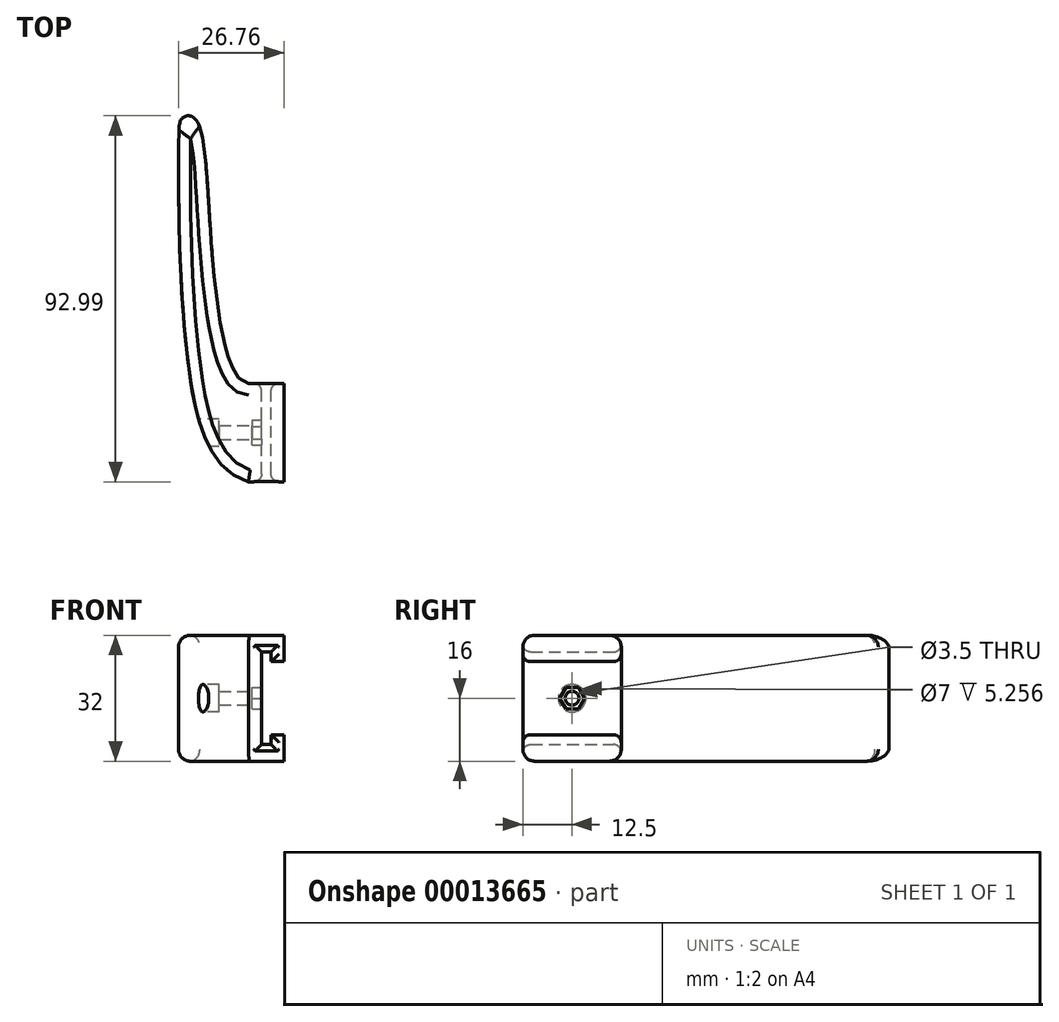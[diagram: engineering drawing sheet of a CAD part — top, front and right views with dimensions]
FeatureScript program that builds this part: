
annotation { "Feature Type Name" : "Feature", "Feature Type Description" : "" }
export const myFeature = defineFeature(function(context is Context, id is Id, definition is map)
    precondition{}
    {
        {
            var Q0;
            Q0=qCreatedBy(makeId("Front.planeOp"),FACE);
            var sketch = newSketch(context, id + "F0", { "sketchPlane" : qUnion([Q0])});
            skLineSegment(sketch, "E0", {"start": v(-4.57, 0) * mm, "end": v(-4.57, 16) * mm});
            skLineSegment(sketch, "E1", {"start": v(-4.57, 16) * mm, "end": v(4.43, 16) * mm});
            skLineSegment(sketch, "E2", {"start": v(4.43, 16) * mm, "end": v(4.43, 9.3) * mm});
            skLineSegment(sketch, "E3", {"start": v(4.43, 9.3) * mm, "end": v(1.18, 9.3) * mm});
            skLineSegment(sketch, "E4", {"start": v(1.18, 9.3) * mm, "end": v(1.18, 11.75) * mm});
            skLineSegment(sketch, "E5", {"start": v(1.18, 11.75) * mm, "end": v(-1.22, 11.75) * mm});
            skLineSegment(sketch, "E6", {"start": v(-1.22, 11.75) * mm, "end": v(-1.22, 0) * mm});
            skLineSegment(sketch, "E7", {"start": v(-1.22, 0) * mm, "end": v(-4.57, 0) * mm});
            skSolve(sketch);
        }
        {
            var Q0;
            Q0=makeQuery(id+"F0.imprint","IMPRINT",FACE,{"disambiguationData":[TD([[makeQuery(id+"F0.imprint","IMPRINT",EDGE,{"derivedFrom":sQuery(id+"F0.wireOp",EDGE,"E0")}),-1.0]])]});
            extrude(context, id + "F1", {"entities" : qUnion([Q0]), "depth" : 25 * mm});
        }
        {
            var Q0;
            Q0=makeQuery(id+"F1.opExtrude","SWEPT_BODY",BODY,{"disambiguationData":[OSD([sQuery(id+"F0.wireOp",EDGE,"E0"),sQuery(id+"F0.wireOp",EDGE,"E1"),sQuery(id+"F0.wireOp",EDGE,"E2"),sQuery(id+"F0.wireOp",EDGE,"E3"),sQuery(id+"F0.wireOp",EDGE,"E4"),sQuery(id+"F0.wireOp",EDGE,"E5"),sQuery(id+"F0.wireOp",EDGE,"E6"),sQuery(id+"F0.wireOp",EDGE,"E7")])]});
            var Q1;
            Q1=qCreatedBy(makeId("Top.planeOp"),FACE);
            mirror(context, id + "F2", {"operationType" : NewBodyOperationType.ADD, "entities" : qUnion([Q0]), "mirrorPlane" : qUnion([Q1])});
        }
        {
            var Q0;
            Q0=qCreatedBy(makeId("Top.planeOp"),FACE);
            var sketch = newSketch(context, id + "F3", { "sketchPlane" : qUnion([Q0])});
            skFitSpline(sketch, "E8", {"points": [v(-4.57, -25) * mm, v(-17.08, -9.6) * mm, v(-22.3, 61.46) * mm, v(-21.16, 67.57) * mm, v(-18.35, 67.44) * mm, v(-14.03, 36.03) * mm, v(-4.57, 0) * mm], "startDerivative": vector(-102.38, 29.96) * mm, "endDerivative": vector(82.11, 0) * mm});
            skLineSegment(sketch, "E9", {"start": v(-4.57, -25) * mm, "end": v(-4.57, 0) * mm});
            skSolve(sketch);
        }
        {
            var Q0;
            Q0=makeQuery(id+"F3.imprint","IMPRINT",FACE,{"disambiguationData":[TD([[makeQuery(id+"F3.imprint","IMPRINT",EDGE,{"derivedFrom":sQuery(id+"F3.wireOp",EDGE,"E8")}),-1.0]])]});
            extrude(context, id + "F4", {"entities" : qUnion([Q0]), "operationType" : NewBodyOperationType.ADD, "depth" : 16 * mm, "hasSecondDirection" : true, "secondDirectionOppositeDirection" : true, "secondDirectionDepth" : 16 * mm});
        }
        {
            var Q0;
            Q0=makeQuery(id+"F4.opExtrude","CAP_EDGE",EDGE,{"disambiguationData":[OSD([sQuery(id+"F3.wireOp",EDGE,"E8")])],"isStart":true});
            var Q1;
            Q1=makeQuery(id+"F4.opExtrude","CAP_EDGE",EDGE,{"disambiguationData":[OSD([sQuery(id+"F3.wireOp",EDGE,"E8")])],"isStart":false});
            var Q2;
            Q2=makeQuery(id+"F2.opPattern","COPY",EDGE,{"derivedFrom":makeQuery(id+"F1.opExtrude","CAP_EDGE",EDGE,{"disambiguationData":[OSD([sQuery(id+"F0.wireOp",EDGE,"E1")])],"isStart":true}),"instanceName":"1"});
            var Q3;
            Q3=makeQuery(id+"F2.opPattern","COPY",EDGE,{"derivedFrom":makeQuery(id+"F1.opExtrude","CAP_EDGE",EDGE,{"disambiguationData":[OSD([sQuery(id+"F0.wireOp",EDGE,"E1")])],"isStart":false}),"instanceName":"1"});
            var Q4;
            Q4=makeQuery(id+"F1.opExtrude","CAP_EDGE",EDGE,{"disambiguationData":[OSD([sQuery(id+"F0.wireOp",EDGE,"E1")])],"isStart":true});
            var Q5;
            Q5=makeQuery(id+"F1.opExtrude","CAP_EDGE",EDGE,{"disambiguationData":[OSD([sQuery(id+"F0.wireOp",EDGE,"E1")])],"isStart":false});
            fillet(context, id + "F5", {"entities" : qUnion([Q0, Q1, Q2, Q3, Q4, Q5]), "radius" : 3 * mm, "tangentPropagation" : true, "allowEdgeOverflow" : false});
        }
        {
            var Q0;
            Q0=makeQuery(id+"F1.opExtrude","CAP_EDGE",EDGE,{"disambiguationData":[OSD([sQuery(id+"F0.wireOp",EDGE,"E5")])],"isStart":true});
            var Q1;
            Q1=makeQuery(id+"F2.opPattern","COPY",EDGE,{"derivedFrom":makeQuery(id+"F1.opExtrude","CAP_EDGE",EDGE,{"disambiguationData":[OSD([sQuery(id+"F0.wireOp",EDGE,"E5")])],"isStart":true}),"instanceName":"1"});
            var Q2;
            Q2=makeQuery(id+"F2.opPattern","COPY",EDGE,{"derivedFrom":makeQuery(id+"F1.opExtrude","CAP_EDGE",EDGE,{"disambiguationData":[OSD([sQuery(id+"F0.wireOp",EDGE,"E4")])],"isStart":true}),"instanceName":"1"});
            var Q3;
            Q3=makeQuery(id+"F1.opExtrude","CAP_EDGE",EDGE,{"disambiguationData":[OSD([sQuery(id+"F0.wireOp",EDGE,"E4")])],"isStart":true});
            var Q4;
            {var subQ0=makeQuery(id+"F1.opExtrude","CAP_EDGE",EDGE,{"disambiguationData":[OSD([sQuery(id+"F0.wireOp",EDGE,"E6")])],"isStart":true});Q4=makeQuery(id+"F2.boolean.opBoolean","MERGE",EDGE,{"derivedFrom":[subQ0,makeQuery(id+"F2.opPattern","COPY",EDGE,{"derivedFrom":subQ0,"instanceName":"1"})]});}
            var Q5;
            {var subQ0=makeQuery(id+"F1.opExtrude","CAP_EDGE",EDGE,{"disambiguationData":[OSD([sQuery(id+"F0.wireOp",EDGE,"E6")])],"isStart":false});Q5=makeQuery(id+"F2.boolean.opBoolean","MERGE",EDGE,{"derivedFrom":[subQ0,makeQuery(id+"F2.opPattern","COPY",EDGE,{"derivedFrom":subQ0,"instanceName":"1"})]});}
            var Q6;
            Q6=makeQuery(id+"F2.opPattern","COPY",EDGE,{"derivedFrom":makeQuery(id+"F1.opExtrude","CAP_EDGE",EDGE,{"disambiguationData":[OSD([sQuery(id+"F0.wireOp",EDGE,"E5")])],"isStart":false}),"instanceName":"1"});
            var Q7;
            Q7=makeQuery(id+"F1.opExtrude","CAP_EDGE",EDGE,{"disambiguationData":[OSD([sQuery(id+"F0.wireOp",EDGE,"E5")])],"isStart":false});
            var Q8;
            Q8=makeQuery(id+"F2.opPattern","COPY",EDGE,{"derivedFrom":makeQuery(id+"F1.opExtrude","CAP_EDGE",EDGE,{"disambiguationData":[OSD([sQuery(id+"F0.wireOp",EDGE,"E3")])],"isStart":false}),"instanceName":"1"});
            var Q9;
            Q9=makeQuery(id+"F1.opExtrude","CAP_EDGE",EDGE,{"disambiguationData":[OSD([sQuery(id+"F0.wireOp",EDGE,"E3")])],"isStart":false});
            var Q10;
            Q10=makeQuery(id+"F2.opPattern","COPY",EDGE,{"derivedFrom":makeQuery(id+"F1.opExtrude","CAP_EDGE",EDGE,{"disambiguationData":[OSD([sQuery(id+"F0.wireOp",EDGE,"E4")])],"isStart":false}),"instanceName":"1"});
            var Q11;
            Q11=makeQuery(id+"F1.opExtrude","CAP_EDGE",EDGE,{"disambiguationData":[OSD([sQuery(id+"F0.wireOp",EDGE,"E4")])],"isStart":false});
            var Q12;
            Q12=makeQuery(id+"F1.opExtrude","CAP_EDGE",EDGE,{"disambiguationData":[OSD([sQuery(id+"F0.wireOp",EDGE,"E3")])],"isStart":true});
            var Q13;
            Q13=makeQuery(id+"F2.opPattern","COPY",EDGE,{"derivedFrom":makeQuery(id+"F1.opExtrude","CAP_EDGE",EDGE,{"disambiguationData":[OSD([sQuery(id+"F0.wireOp",EDGE,"E3")])],"isStart":true}),"instanceName":"1"});
            fillet(context, id + "F6", {"entities" : qUnion([Q0, Q1, Q2, Q3, Q4, Q5, Q6, Q7, Q8, Q9, Q10, Q11, Q12, Q13]), "radius" : 2 * mm, "tangentPropagation" : true, "allowEdgeOverflow" : false});
        }
        {
            var Q0;
            {var subQ0=makeQuery(id+"F1.opExtrude","SWEPT_FACE",FACE,{"disambiguationData":[OSD([sQuery(id+"F0.wireOp",EDGE,"E6")])]});Q0=makeQuery(id+"F2.boolean.opBoolean","MERGE",FACE,{"derivedFrom":[subQ0,makeQuery(id+"F2.opPattern","COPY",FACE,{"derivedFrom":subQ0,"instanceName":"1"})]});}
            var sketch = newSketch(context, id + "F7", { "sketchPlane" : qUnion([Q0])});
            skCircle(sketch, "E10.cCircle", {"center": v(-12.5, 0) * mm, "radius": 2.75 * mm, "construction": true});
            skLineSegment(sketch, "E10.0", {"start": v(-15.68, 0) * mm, "end": v(-14.09, 2.75) * mm});
            skLineSegment(sketch, "E10.1", {"start": v(-14.09, 2.75) * mm, "end": v(-10.91, 2.75) * mm});
            skLineSegment(sketch, "E10.2", {"start": v(-10.91, 2.75) * mm, "end": v(-9.32, 0) * mm});
            skLineSegment(sketch, "E10.3", {"start": v(-9.32, 0) * mm, "end": v(-10.91, -2.75) * mm});
            skLineSegment(sketch, "E10.4", {"start": v(-10.91, -2.75) * mm, "end": v(-14.09, -2.75) * mm});
            skLineSegment(sketch, "E10.5", {"start": v(-14.09, -2.75) * mm, "end": v(-15.68, 0) * mm});
            skPoint(sketch, "E10.0.midPoint", {"position": v(-14.88, 1.37) * mm});
            skLineSegment(sketch, "E11", {"start": v(-2, 0) * mm, "end": v(-23, 0) * mm, "construction": true});
            skSolve(sketch);
        }
        {
            var Q0;
            Q0 = qSketchRegion(id + "F7", true);
            extrude(context, id + "F8", {"entities" : qUnion([Q0]), "operationType" : NewBodyOperationType.REMOVE, "oppositeDirection" : true, "depth" : 2.4 * mm});
        }
        {
            var Q0;
            Q0=makeQuery(id+"F8.boolean.opBoolean","COPY",FACE,{"derivedFrom":makeQuery(id+"F8.opExtrude","CAP_FACE",FACE,{"disambiguationData":[OSD([sQuery(id+"F7.wireOp",EDGE,"E10.0"),sQuery(id+"F7.wireOp",EDGE,"E10.1"),sQuery(id+"F7.wireOp",EDGE,"E10.2"),sQuery(id+"F7.wireOp",EDGE,"E10.3"),sQuery(id+"F7.wireOp",EDGE,"E10.4"),sQuery(id+"F7.wireOp",EDGE,"E10.5")])],"isStart":false})});
            var sketch = newSketch(context, id + "F9", { "sketchPlane" : qUnion([Q0])});
            skCircle(sketch, "E12", {"center": v(-12.5, 0) * mm, "radius": 1.75 * mm});
            skLineSegment(sketch, "E13", {"start": v(-15.68, 0) * mm, "end": v(-9.32, 0) * mm, "construction": true});
            skSolve(sketch);
        }
        {
            var Q0;
            Q0 = qSketchRegion(id + "F9", true);
            extrude(context, id + "F10", {"entities" : qUnion([Q0]), "operationType" : NewBodyOperationType.REMOVE, "oppositeDirection" : true, "depth" : 25 * mm});
        }
        {
            var Q0;
            Q0=qCreatedBy(makeId("Right.planeOp"),FACE);
            cPlane(context, id + "F11", {"entities" : qUnion([Q0]), "cplaneType" : CPlaneType.OFFSET, "offset" : 20 * mm, "oppositeDirection" : true, "width" : 150 * mm, "height" : 150 * mm});
        }
        {
            var Q0;
            Q0=qCreatedBy(id+"F11.planeOp",FACE);
            var sketch = newSketch(context, id + "F12", { "sketchPlane" : qUnion([Q0])});
            skCircle(sketch, "E14", {"center": v(-12.5, 0) * mm, "radius": 3.5 * mm});
            skSolve(sketch);
        }
        {
            var Q0;
            Q0 = qSketchRegion(id + "F12", true);
            extrude(context, id + "F13", {"entities" : qUnion([Q0]), "operationType" : NewBodyOperationType.REMOVE, "depth" : 8 * mm});
        }
    });
